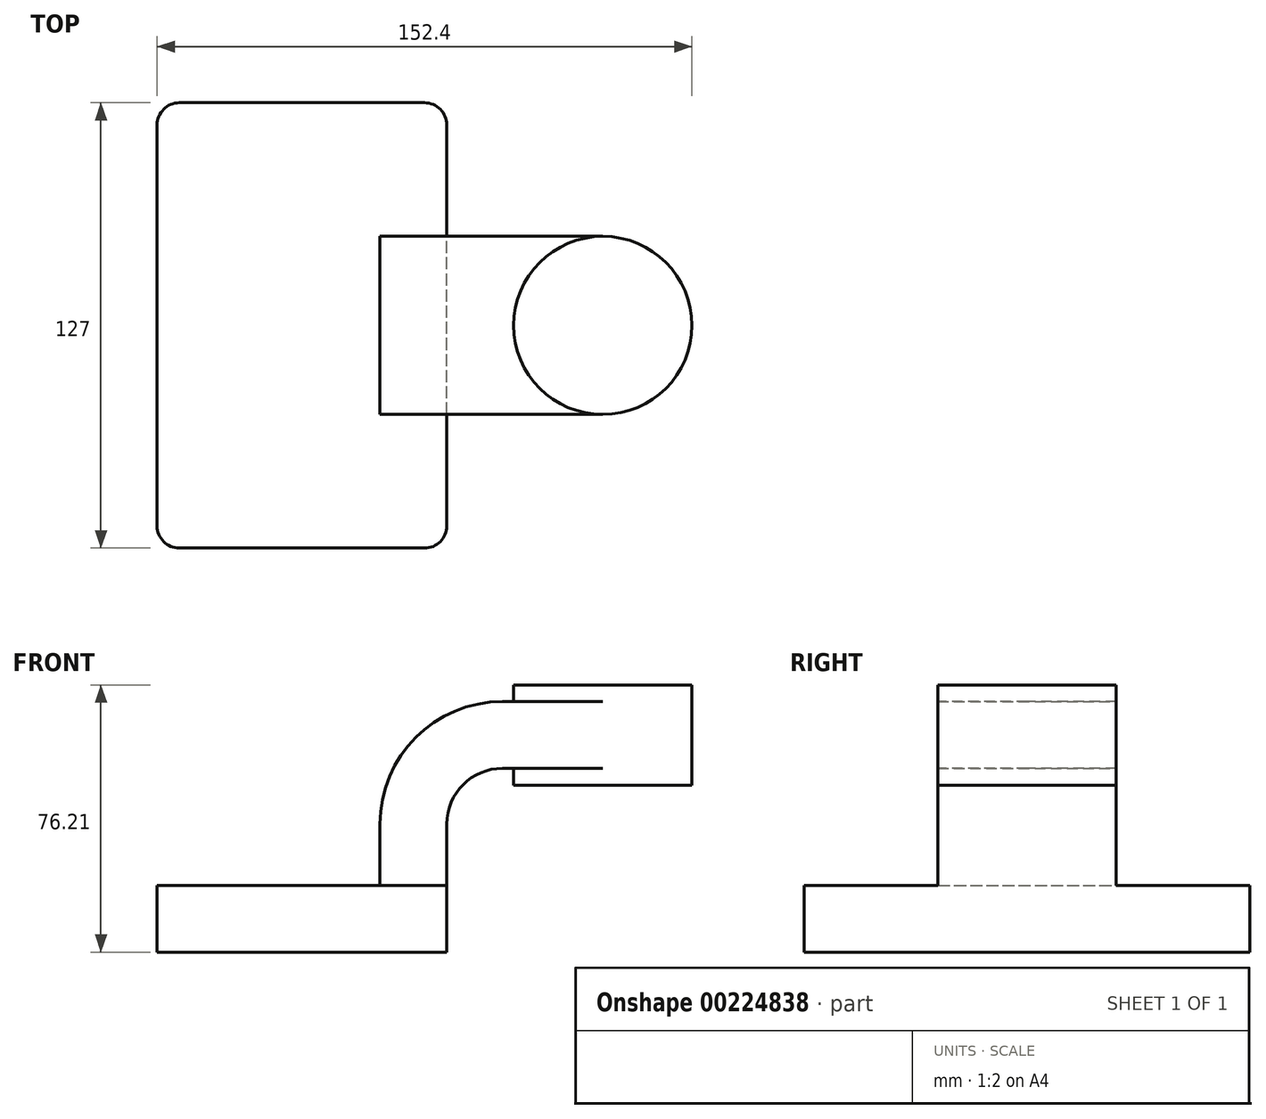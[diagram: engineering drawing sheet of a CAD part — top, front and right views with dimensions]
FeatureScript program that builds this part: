
annotation { "Feature Type Name" : "Feature", "Feature Type Description" : "" }
export const myFeature = defineFeature(function(context is Context, id is Id, definition is map)
    precondition{}
    {
        {
            var Q0;
            Q0=qCreatedBy(makeId("Front.planeOp"),FACE);
            var sketch = newSketch(context, id + "F0", { "sketchPlane" : qUnion([Q0])});
            skLineSegment(sketch, "E0.bottom", {"start": v(-41.28, 9.52) * mm, "end": v(41.27, 9.53) * mm});
            skLineSegment(sketch, "E0.top", {"start": v(-41.28, -9.53) * mm, "end": v(41.28, -9.53) * mm});
            skLineSegment(sketch, "E0.left", {"start": v(-41.28, 9.52) * mm, "end": v(-41.27, -9.53) * mm});
            skLineSegment(sketch, "E0.right", {"start": v(41.28, 9.53) * mm, "end": v(41.28, -9.52) * mm});
            skPoint(sketch, "E0.middle", {"position": v(0, 0) * mm});
            skLineSegment(sketch, "E1.bottom", {"start": v(60.33, 66.68) * mm, "end": v(111.13, 66.68) * mm});
            skLineSegment(sketch, "E1.top", {"start": v(60.33, 38.1) * mm, "end": v(111.13, 38.1) * mm});
            skLineSegment(sketch, "E1.left", {"start": v(60.33, 66.68) * mm, "end": v(60.33, 38.1) * mm});
            skLineSegment(sketch, "E1.right", {"start": v(111.13, 66.68) * mm, "end": v(111.13, 38.1) * mm});
            skPoint(sketch, "E1.middle", {"position": v(85.73, 52.39) * mm});
            skLineSegment(sketch, "E2", {"start": v(41.27, 9.53) * mm, "end": v(41.27, 27) * mm});
            skArc(sketch, "E3", {"start": v(41.27, 27) * mm, "mid": v(45.92, 38.23) * mm, "end": v(57.15, 42.88) * mm});
            skLineSegment(sketch, "E4", {"start": v(57.15, 42.88) * mm, "end": v(85.73, 42.88) * mm});
            skLineSegment(sketch, "E5.0", {"start": v(57.15, 61.93) * mm, "end": v(85.73, 61.93) * mm});
            skArc(sketch, "E5.1", {"start": v(22.22, 27) * mm, "mid": v(32.45, 51.7) * mm, "end": v(57.15, 61.93) * mm});
            skLineSegment(sketch, "E5.2", {"start": v(22.22, 9.53) * mm, "end": v(22.22, 27) * mm});
            skLineSegment(sketch, "E6", {"start": v(85.73, 38.1) * mm, "end": v(85.73, 66.68) * mm});
            skFitSpline(sketch, "E7", {"points": [v(-41.28, 9.53) * mm, v(57.15, 61.93) * mm], "startDerivative": vector(49.55, 116.18) * mm, "endDerivative": vector(105.27, -19.98) * mm});
            skSolve(sketch);
        }
        {
            var Q0;
            Q0=makeQuery(id+"F0.imprint","IMPRINT",FACE,{"disambiguationData":[TD([[makeQuery(id+"F0.imprint","IMPRINT",EDGE,{"derivedFrom":sQuery(id+"F0.wireOp",EDGE,"E0.top")}),1.0]])]});
            extrude(context, id + "F1", {"entities" : qUnion([Q0]), "depth" : 127 * mm, "symmetric" : true});
        }
        {
            var Q0;
            {var subQ1=sQuery(id+"F0.wireOp",EDGE,"E2");Q0=makeQuery(id+"F0.imprint","IMPRINT",FACE,{"disambiguationData":[TD([[makeQuery(id+"F0.imprint","IMPRINT",EDGE,{"derivedFrom":subQ1}),1.0]])]});}
            var Q1;
            {var subQ0=sQuery(id+"F0.wireOp",EDGE,"E5.0");var subQ1=sQuery(id+"F0.wireOp",EDGE,"E1.left");var subQ2=makeQuery(id+"F0.imprint","INTERSECT",VERTEX,{"derivedFrom":[subQ1,subQ0]});Q1=makeQuery(id+"F0.imprint","IMPRINT",FACE,{"disambiguationData":[TD([[makeQuery(id+"F0.imprint","IMPRINT",EDGE,{"disambiguationData":[TD([[subQ2,-1.0]])],"derivedFrom":subQ1}),1.0]])]});}
            extrude(context, id + "F2", {"entities" : qUnion([Q0, Q1]), "operationType" : NewBodyOperationType.ADD, "depth" : 50.8 * mm, "symmetric" : true});
        }
        {
            var Q0;
            Q0=makeQuery(id+"F0.imprint","IMPRINT",FACE,{"disambiguationData":[TD([[makeQuery(id+"F0.imprint","IMPRINT",EDGE,{"derivedFrom":sQuery(id+"F0.wireOp",EDGE,"E5.1")}),1.0]])]});
            extrude(context, id + "F3", {"entities" : qUnion([Q0]), "operationType" : NewBodyOperationType.ADD, "depth" : 15.88 * mm, "symmetric" : true});
        }
        {
            var Q0;
            {var subQ0=sQuery(id+"F0.wireOp",EDGE,"E1.right");Q0=makeQuery(id+"F0.imprint","IMPRINT",FACE,{"disambiguationData":[TD([[makeQuery(id+"F0.imprint","IMPRINT",EDGE,{"derivedFrom":subQ0}),-1.0]])]});}
            var Q1;
            Q1=sQuery(id+"F0.wireOp",EDGE,"E6");
            revolve(context, id + "F4", {"operationType" : NewBodyOperationType.ADD, "entities" : qUnion([Q0]), "axis" : qUnion([Q1]), "revolveType" : RevolveType.FULL});
        }
        {
            var Q0;
            Q0=makeQuery(id+"F1.opExtrude","CAP_EDGE",EDGE,{"disambiguationData":[OSD([sQuery(id+"F0.wireOp",EDGE,"E0.left")])],"isStart":false});
            var Q1;
            Q1=makeQuery(id+"F1.opExtrude","CAP_EDGE",EDGE,{"disambiguationData":[OSD([sQuery(id+"F0.wireOp",EDGE,"E0.right")])],"isStart":false});
            var Q2;
            Q2=makeQuery(id+"F1.opExtrude","CAP_EDGE",EDGE,{"disambiguationData":[OSD([sQuery(id+"F0.wireOp",EDGE,"E0.right")])],"isStart":true});
            var Q3;
            Q3=makeQuery(id+"F1.opExtrude","CAP_EDGE",EDGE,{"disambiguationData":[OSD([sQuery(id+"F0.wireOp",EDGE,"E0.left")])],"isStart":true});
            fillet(context, id + "F5", {"entities" : qUnion([Q0, Q1, Q2, Q3]), "radius" : 6.35 * mm, "tangentPropagation" : true, "allowEdgeOverflow" : false});
        }
    });
